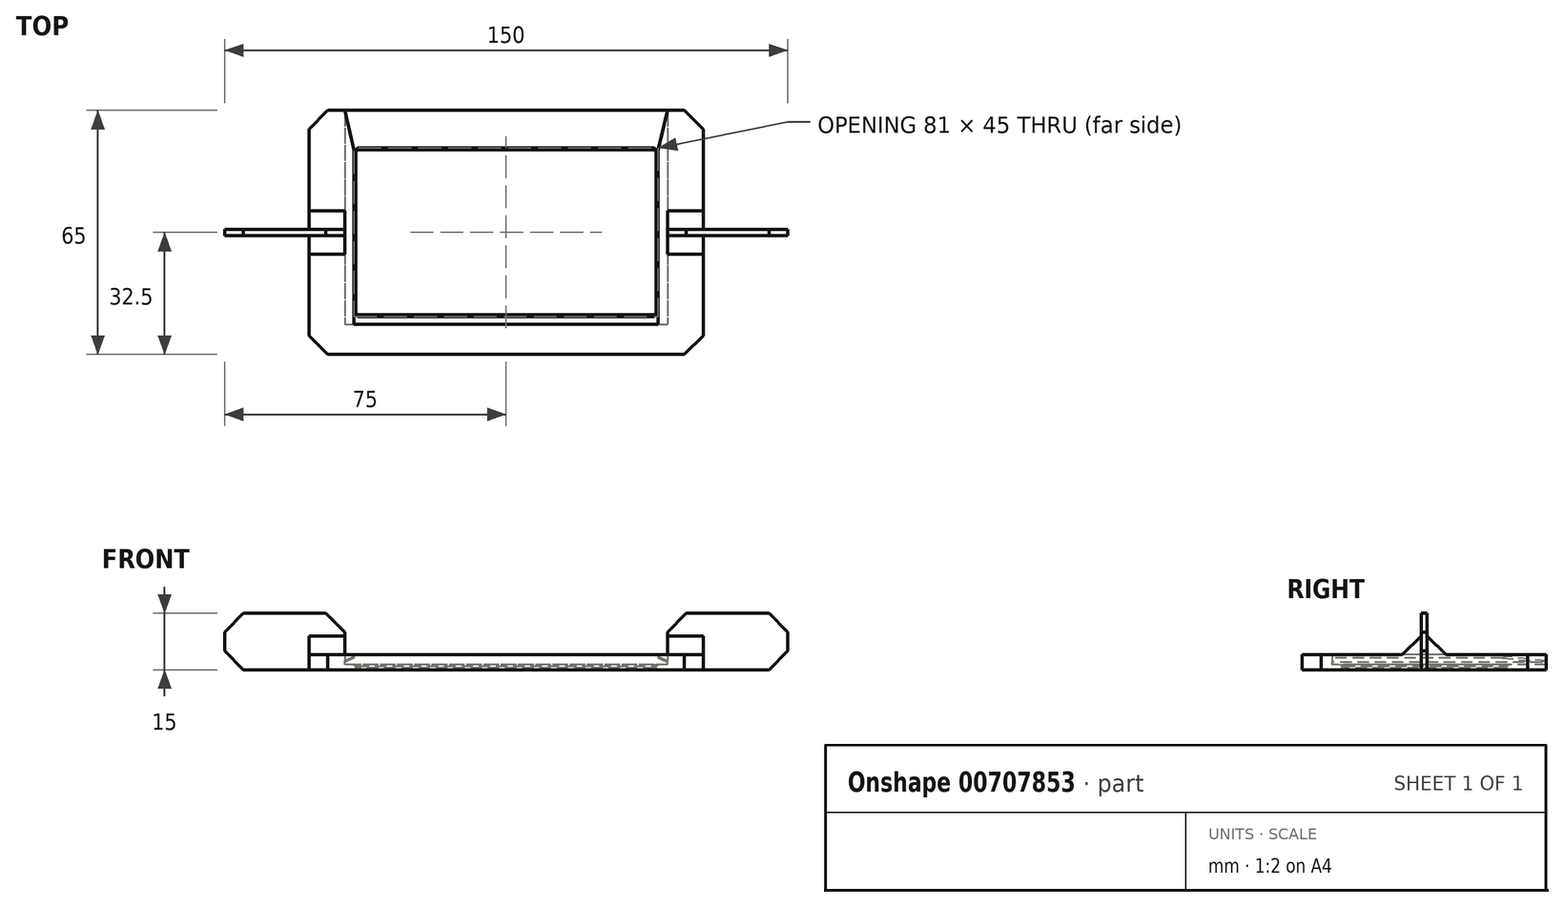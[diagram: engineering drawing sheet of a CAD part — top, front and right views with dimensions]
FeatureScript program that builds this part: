
annotation { "Feature Type Name" : "Feature", "Feature Type Description" : "" }
export const myFeature = defineFeature(function(context is Context, id is Id, definition is map)
    precondition{}
    {
        {
            var Q0;
            Q0=qCreatedBy(makeId("Top.planeOp"),FACE);
            var sketch = newSketch(context, id + "F0", { "sketchPlane" : qUnion([Q0])});
            skLineSegment(sketch, "E0.bottom", {"start": v(40, -22) * mm, "end": v(-40, -22) * mm});
            skLineSegment(sketch, "E0.top", {"start": v(40, 22) * mm, "end": v(-40, 22) * mm});
            skLineSegment(sketch, "E0.left", {"start": v(40, -22) * mm, "end": v(40, 22) * mm});
            skLineSegment(sketch, "E0.right", {"start": v(-40, -22) * mm, "end": v(-40, 22) * mm});
            skPoint(sketch, "E0.middle", {"position": v(0, 0) * mm});
            skLineSegment(sketch, "E1.bottom", {"start": v(52.5, -32.5) * mm, "end": v(-52.5, -32.5) * mm});
            skLineSegment(sketch, "E1.top", {"start": v(52.5, 32.5) * mm, "end": v(-52.5, 32.5) * mm});
            skLineSegment(sketch, "E1.left", {"start": v(52.5, -32.5) * mm, "end": v(52.5, 32.5) * mm});
            skLineSegment(sketch, "E1.right", {"start": v(-52.5, -32.5) * mm, "end": v(-52.5, 32.5) * mm});
            skSolve(sketch);
        }
        {
            var Q0;
            Q0 = qSketchRegion(id + "F0", true);
            extrude(context, id + "F1", {"entities" : qUnion([Q0]), "depth" : 2 * mm, "offsetDistance" : 25 * mm});
        }
        {
            var Q0;
            Q0=makeQuery(id+"F1.opExtrude","CAP_FACE",FACE,{"disambiguationData":[OSD([sQuery(id+"F0.wireOp",EDGE,"E0.bottom"),sQuery(id+"F0.wireOp",EDGE,"E0.top"),sQuery(id+"F0.wireOp",EDGE,"E0.left"),sQuery(id+"F0.wireOp",EDGE,"E0.right"),sQuery(id+"F0.wireOp",EDGE,"E1.bottom"),sQuery(id+"F0.wireOp",EDGE,"E1.top"),sQuery(id+"F0.wireOp",EDGE,"E1.left"),sQuery(id+"F0.wireOp",EDGE,"E1.right")])],"isStart":false});
            var sketch = newSketch(context, id + "F2", { "sketchPlane" : qUnion([Q0])});
            skLineSegment(sketch, "E2.bottom", {"start": v(-43, 32.5) * mm, "end": v(43, 32.5) * mm});
            skLineSegment(sketch, "E2.top", {"start": v(-43, -24.5) * mm, "end": v(43, -24.5) * mm});
            skLineSegment(sketch, "E2.left", {"start": v(-43, 32.5) * mm, "end": v(-43, -24.5) * mm});
            skLineSegment(sketch, "E2.right", {"start": v(43, 32.5) * mm, "end": v(43, -24.5) * mm});
            skSolve(sketch);
        }
        {
            var Q0;
            Q0 = qSketchRegion(id + "F2", true);
            extrude(context, id + "F3", {"entities" : qUnion([Q0]), "operationType" : NewBodyOperationType.REMOVE, "oppositeDirection" : true, "depth" : 0.6 * mm, "offsetDistance" : 25 * mm});
        }
        {
            var Q0;
            Q0=makeQuery(id+"F1.opExtrude","CAP_FACE",FACE,{"disambiguationData":[OSD([sQuery(id+"F0.wireOp",EDGE,"E0.bottom"),sQuery(id+"F0.wireOp",EDGE,"E0.top"),sQuery(id+"F0.wireOp",EDGE,"E0.left"),sQuery(id+"F0.wireOp",EDGE,"E0.right"),sQuery(id+"F0.wireOp",EDGE,"E1.bottom"),sQuery(id+"F0.wireOp",EDGE,"E1.top"),sQuery(id+"F0.wireOp",EDGE,"E1.left"),sQuery(id+"F0.wireOp",EDGE,"E1.right")])],"isStart":false});
            var sketch = newSketch(context, id + "F4", { "sketchPlane" : qUnion([Q0])});
            skLineSegment(sketch, "E3", {"start": v(-52.5, 32.5) * mm, "end": v(-43, 32.5) * mm});
            skLineSegment(sketch, "E4", {"start": v(-43, 32.5) * mm, "end": v(-40.5, 22) * mm});
            skLineSegment(sketch, "E5", {"start": v(-40.5, 22) * mm, "end": v(-40.5, -24.5) * mm});
            skLineSegment(sketch, "E6", {"start": v(-40.5, -24.5) * mm, "end": v(40.5, -24.5) * mm});
            skLineSegment(sketch, "E7", {"start": v(52.5, -32.5) * mm, "end": v(-52.5, -32.5) * mm});
            skLineSegment(sketch, "E8", {"start": v(-52.5, -32.5) * mm, "end": v(-52.5, 32.5) * mm});
            skLineSegment(sketch, "E9.MirrorCS", {"start": v(52.5, -32.5) * mm, "end": v(52.5, 32.5) * mm});
            skLineSegment(sketch, "E10.MirrorCS", {"start": v(52.5, 32.5) * mm, "end": v(43, 32.5) * mm});
            skLineSegment(sketch, "E11.MirrorCS", {"start": v(40.5, 22) * mm, "end": v(40.5, -24.5) * mm});
            skLineSegment(sketch, "E12.MirrorCS", {"start": v(43, 32.5) * mm, "end": v(40.5, 22) * mm});
            skSolve(sketch);
        }
        {
            var Q0;
            Q0 = qSketchRegion(id + "F4", true);
            extrude(context, id + "F5", {"entities" : qUnion([Q0]), "operationType" : NewBodyOperationType.ADD, "depth" : 2 * mm, "offsetDistance" : 25 * mm});
        }
        {
            var Q0;
            Q0=makeQuery(id+"F5.boolean.opBoolean","MERGE",FACE,{"derivedFrom":[makeQuery(id+"F3.boolean.opBoolean","COPY",FACE,{"derivedFrom":makeQuery(id+"F3.opExtrude","SWEPT_FACE",FACE,{"disambiguationData":[OSD([sQuery(id+"F2.wireOp",EDGE,"E2.top")])]})}),makeQuery(id+"F5.opExtrude","SWEPT_FACE",FACE,{"disambiguationData":[OSD([sQuery(id+"F4.wireOp",EDGE,"E6")])]})]});
            var sketch = newSketch(context, id + "F6", { "sketchPlane" : qUnion([Q0])});
            skLineSegment(sketch, "E13", {"start": v(43, 2) * mm, "end": v(40.5, 2) * mm});
            skLineSegment(sketch, "E14", {"start": v(40.5, 2) * mm, "end": v(40.5, 3.17) * mm});
            skLineSegment(sketch, "E15", {"start": v(40.5, 3.17) * mm, "end": v(43, 2) * mm});
            skLineSegment(sketch, "E16.MirrorCS", {"start": v(-43, 2) * mm, "end": v(-40.5, 2) * mm});
            skLineSegment(sketch, "E17.MirrorCS", {"start": v(-40.5, 2) * mm, "end": v(-40.5, 3.17) * mm});
            skLineSegment(sketch, "E18.MirrorCS", {"start": v(-40.5, 3.17) * mm, "end": v(-43, 2) * mm});
            skSolve(sketch);
        }
        {
            var Q0;
            Q0 = qSketchRegion(id + "F6", true);
            extrude(context, id + "F7", {"entities" : qUnion([Q0]), "operationType" : NewBodyOperationType.REMOVE, "endBound" : BoundingType.THROUGH_ALL, "depth" : 25 * mm, "offsetDistance" : 25 * mm});
        }
        {
            var Q0;
            Q0=qCreatedBy(makeId("Top.planeOp"),FACE);
            var sketch = newSketch(context, id + "F8", { "sketchPlane" : qUnion([Q0])});
            skLineSegment(sketch, "E19.bottom", {"start": v(-75, 0.8) * mm, "end": v(-43, 0.8) * mm});
            skLineSegment(sketch, "E19.top", {"start": v(-75, -0.8) * mm, "end": v(-43, -0.8) * mm});
            skLineSegment(sketch, "E19.left", {"start": v(-75, 0.8) * mm, "end": v(-75, -0.8) * mm});
            skLineSegment(sketch, "E19.right", {"start": v(-43, 0.8) * mm, "end": v(-43, -0.8) * mm});
            skLineSegment(sketch, "E20.MirrorCS", {"start": v(75, -0.8) * mm, "end": v(43, -0.8) * mm});
            skLineSegment(sketch, "E21.MirrorCS", {"start": v(43, 0.8) * mm, "end": v(43, -0.8) * mm});
            skLineSegment(sketch, "E22.MirrorCS", {"start": v(75, 0.8) * mm, "end": v(43, 0.8) * mm});
            skLineSegment(sketch, "E23.MirrorCS", {"start": v(75, 0.8) * mm, "end": v(75, -0.8) * mm});
            skSolve(sketch);
        }
        {
            var Q0;
            Q0 = qSketchRegion(id + "F8", true);
            extrude(context, id + "F9", {"entities" : qUnion([Q0]), "operationType" : NewBodyOperationType.ADD, "depth" : 15 * mm, "offsetDistance" : 25 * mm});
        }
        {
            var Q0;
            Q0=makeQuery(id+"F9.opExtrude","CAP_EDGE",EDGE,{"disambiguationData":[OSD([sQuery(id+"F8.wireOp",EDGE,"E19.left")])],"isStart":false});
            var Q1;
            Q1=makeQuery(id+"F9.opExtrude","CAP_EDGE",EDGE,{"disambiguationData":[OSD([sQuery(id+"F8.wireOp",EDGE,"E19.right")])],"isStart":false});
            var Q2;
            Q2=makeQuery(id+"F9.opExtrude","CAP_EDGE",EDGE,{"disambiguationData":[OSD([sQuery(id+"F8.wireOp",EDGE,"E19.left")])],"isStart":true});
            var Q3;
            Q3=makeQuery(id+"F5.boolean.opBoolean","MERGE",EDGE,{"derivedFrom":[makeQuery(id+"F1.opExtrude","SWEPT_EDGE",EDGE,{"disambiguationData":[OSD([sQuery(id+"F0.wireOp",EDGE,"E1.bottom"),sQuery(id+"F0.wireOp",EDGE,"E1.right")])]}),makeQuery(id+"F5.opExtrude","SWEPT_EDGE",EDGE,{"disambiguationData":[OSD([sQuery(id+"F4.wireOp",EDGE,"E7"),sQuery(id+"F4.wireOp",EDGE,"E8")])]})]});
            var Q4;
            Q4=makeQuery(id+"F5.boolean.opBoolean","MERGE",EDGE,{"derivedFrom":[makeQuery(id+"F1.opExtrude","SWEPT_EDGE",EDGE,{"disambiguationData":[OSD([sQuery(id+"F0.wireOp",EDGE,"E1.top"),sQuery(id+"F0.wireOp",EDGE,"E1.right")])]}),makeQuery(id+"F5.opExtrude","SWEPT_EDGE",EDGE,{"disambiguationData":[OSD([sQuery(id+"F4.wireOp",EDGE,"E3"),sQuery(id+"F4.wireOp",EDGE,"E8")])]})]});
            var Q5;
            Q5=makeQuery(id+"F9.boolean.opBoolean","INTERSECT",EDGE,{"derivedFrom":[makeQuery(id+"F5.opExtrude","CAP_FACE",FACE,{"disambiguationData":[OSD([sQuery(id+"F4.wireOp",EDGE,"E3"),sQuery(id+"F4.wireOp",EDGE,"E4"),sQuery(id+"F4.wireOp",EDGE,"E5"),sQuery(id+"F4.wireOp",EDGE,"E6"),sQuery(id+"F4.wireOp",EDGE,"E7"),sQuery(id+"F4.wireOp",EDGE,"E8"),sQuery(id+"F4.wireOp",EDGE,"E9.MirrorCS"),sQuery(id+"F4.wireOp",EDGE,"E10.MirrorCS"),sQuery(id+"F4.wireOp",EDGE,"E11.MirrorCS"),sQuery(id+"F4.wireOp",EDGE,"E12.MirrorCS")])],"isStart":false}),makeQuery(id+"F9.opExtrude","SWEPT_FACE",FACE,{"disambiguationData":[OSD([sQuery(id+"F8.wireOp",EDGE,"E19.top")])]})]});
            var Q6;
            Q6=makeQuery(id+"F9.boolean.opBoolean","INTERSECT",EDGE,{"derivedFrom":[makeQuery(id+"F5.opExtrude","CAP_FACE",FACE,{"disambiguationData":[OSD([sQuery(id+"F4.wireOp",EDGE,"E3"),sQuery(id+"F4.wireOp",EDGE,"E4"),sQuery(id+"F4.wireOp",EDGE,"E5"),sQuery(id+"F4.wireOp",EDGE,"E6"),sQuery(id+"F4.wireOp",EDGE,"E7"),sQuery(id+"F4.wireOp",EDGE,"E8"),sQuery(id+"F4.wireOp",EDGE,"E9.MirrorCS"),sQuery(id+"F4.wireOp",EDGE,"E10.MirrorCS"),sQuery(id+"F4.wireOp",EDGE,"E11.MirrorCS"),sQuery(id+"F4.wireOp",EDGE,"E12.MirrorCS")])],"isStart":false}),makeQuery(id+"F9.opExtrude","SWEPT_FACE",FACE,{"disambiguationData":[OSD([sQuery(id+"F8.wireOp",EDGE,"E19.bottom")])]})]});
            var Q7;
            Q7=makeQuery(id+"F9.boolean.opBoolean","INTERSECT",EDGE,{"derivedFrom":[makeQuery(id+"F5.opExtrude","CAP_FACE",FACE,{"disambiguationData":[OSD([sQuery(id+"F4.wireOp",EDGE,"E3"),sQuery(id+"F4.wireOp",EDGE,"E4"),sQuery(id+"F4.wireOp",EDGE,"E5"),sQuery(id+"F4.wireOp",EDGE,"E6"),sQuery(id+"F4.wireOp",EDGE,"E7"),sQuery(id+"F4.wireOp",EDGE,"E8"),sQuery(id+"F4.wireOp",EDGE,"E9.MirrorCS"),sQuery(id+"F4.wireOp",EDGE,"E10.MirrorCS"),sQuery(id+"F4.wireOp",EDGE,"E11.MirrorCS"),sQuery(id+"F4.wireOp",EDGE,"E12.MirrorCS")])],"isStart":false}),makeQuery(id+"F9.opExtrude","SWEPT_FACE",FACE,{"disambiguationData":[OSD([sQuery(id+"F8.wireOp",EDGE,"E20.MirrorCS")])]})]});
            var Q8;
            Q8=makeQuery(id+"F5.boolean.opBoolean","MERGE",EDGE,{"derivedFrom":[makeQuery(id+"F1.opExtrude","SWEPT_EDGE",EDGE,{"disambiguationData":[OSD([sQuery(id+"F0.wireOp",EDGE,"E1.bottom"),sQuery(id+"F0.wireOp",EDGE,"E1.left")])]}),makeQuery(id+"F5.opExtrude","SWEPT_EDGE",EDGE,{"disambiguationData":[OSD([sQuery(id+"F4.wireOp",EDGE,"E7"),sQuery(id+"F4.wireOp",EDGE,"E9.MirrorCS")])]})]});
            var Q9;
            Q9=makeQuery(id+"F5.boolean.opBoolean","MERGE",EDGE,{"derivedFrom":[makeQuery(id+"F1.opExtrude","SWEPT_EDGE",EDGE,{"disambiguationData":[OSD([sQuery(id+"F0.wireOp",EDGE,"E1.top"),sQuery(id+"F0.wireOp",EDGE,"E1.left")])]}),makeQuery(id+"F5.opExtrude","SWEPT_EDGE",EDGE,{"disambiguationData":[OSD([sQuery(id+"F4.wireOp",EDGE,"E9.MirrorCS"),sQuery(id+"F4.wireOp",EDGE,"E10.MirrorCS")])]})]});
            var Q10;
            Q10=makeQuery(id+"F9.boolean.opBoolean","INTERSECT",EDGE,{"derivedFrom":[makeQuery(id+"F5.opExtrude","CAP_FACE",FACE,{"disambiguationData":[OSD([sQuery(id+"F4.wireOp",EDGE,"E3"),sQuery(id+"F4.wireOp",EDGE,"E4"),sQuery(id+"F4.wireOp",EDGE,"E5"),sQuery(id+"F4.wireOp",EDGE,"E6"),sQuery(id+"F4.wireOp",EDGE,"E7"),sQuery(id+"F4.wireOp",EDGE,"E8"),sQuery(id+"F4.wireOp",EDGE,"E9.MirrorCS"),sQuery(id+"F4.wireOp",EDGE,"E10.MirrorCS"),sQuery(id+"F4.wireOp",EDGE,"E11.MirrorCS"),sQuery(id+"F4.wireOp",EDGE,"E12.MirrorCS")])],"isStart":false}),makeQuery(id+"F9.opExtrude","SWEPT_FACE",FACE,{"disambiguationData":[OSD([sQuery(id+"F8.wireOp",EDGE,"E22.MirrorCS")])]})]});
            var Q11;
            Q11=makeQuery(id+"F9.opExtrude","CAP_EDGE",EDGE,{"disambiguationData":[OSD([sQuery(id+"F8.wireOp",EDGE,"E23.MirrorCS")])],"isStart":false});
            var Q12;
            Q12=makeQuery(id+"F9.opExtrude","CAP_EDGE",EDGE,{"disambiguationData":[OSD([sQuery(id+"F8.wireOp",EDGE,"E21.MirrorCS")])],"isStart":false});
            var Q13;
            Q13=makeQuery(id+"F9.opExtrude","CAP_EDGE",EDGE,{"disambiguationData":[OSD([sQuery(id+"F8.wireOp",EDGE,"E23.MirrorCS")])],"isStart":true});
            chamfer(context, id + "F10", {"entities" : qUnion([Q0, Q1, Q2, Q3, Q4, Q5, Q6, Q7, Q8, Q9, Q10, Q11, Q12, Q13]), "width" : 5 * mm, "tangentPropagation" : true});
        }
        {
            var Q0;
            Q0=makeQuery(id+"F1.opExtrude","SWEPT_FACE",FACE,{"disambiguationData":[OSD([sQuery(id+"F0.wireOp",EDGE,"E0.right")])]});
            var Q1;
            Q1=makeQuery(id+"F1.opExtrude","SWEPT_FACE",FACE,{"disambiguationData":[OSD([sQuery(id+"F0.wireOp",EDGE,"E0.left")])]});
            var Q2;
            Q2=makeQuery(id+"F7.boolean.opBoolean","INTERSECT",EDGE,{"derivedFrom":[makeQuery(id+"F5.opExtrude","SWEPT_FACE",FACE,{"disambiguationData":[OSD([sQuery(id+"F4.wireOp",EDGE,"E12.MirrorCS")])]}),makeQuery(id+"F7.opExtrude","SWEPT_FACE",FACE,{"disambiguationData":[OSD([sQuery(id+"F6.wireOp",EDGE,"E18.MirrorCS")])]})]});
            var Q3;
            Q3=makeQuery(id+"F7.boolean.opBoolean","INTERSECT",EDGE,{"derivedFrom":[makeQuery(id+"F5.opExtrude","SWEPT_FACE",FACE,{"disambiguationData":[OSD([sQuery(id+"F4.wireOp",EDGE,"E4")])]}),makeQuery(id+"F7.opExtrude","SWEPT_FACE",FACE,{"disambiguationData":[OSD([sQuery(id+"F6.wireOp",EDGE,"E15")])]})]});
            chamfer(context, id + "F11", {"entities" : qUnion([Q0, Q1, Q2, Q3]), "width" : 0.5 * mm, "tangentPropagation" : true});
        }
    });
